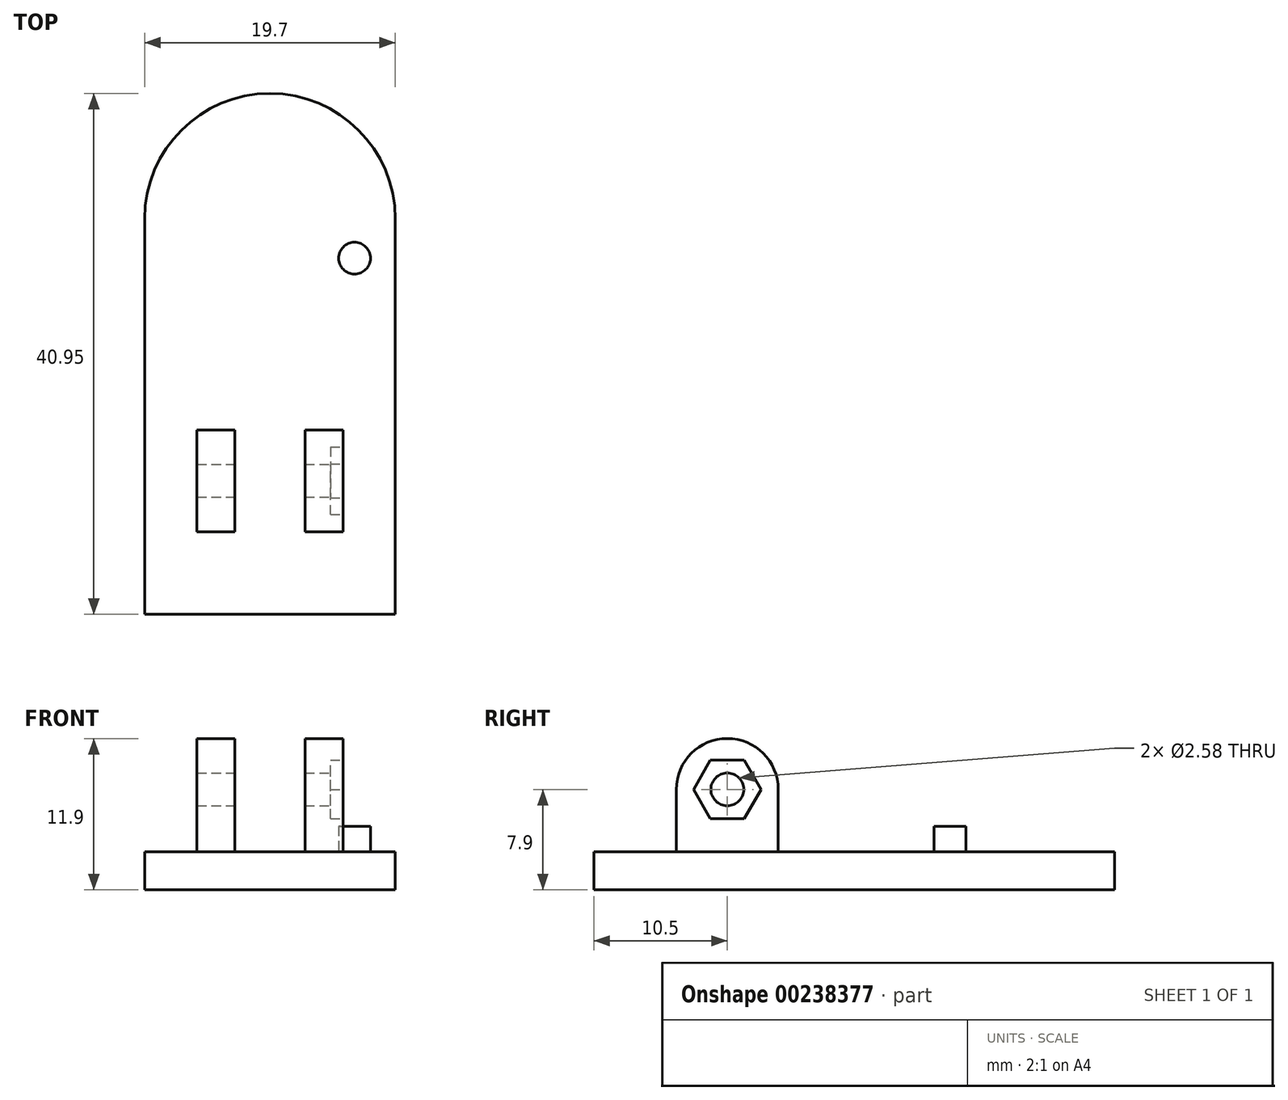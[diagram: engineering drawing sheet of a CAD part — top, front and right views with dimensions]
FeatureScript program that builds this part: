
annotation { "Feature Type Name" : "Feature", "Feature Type Description" : "" }
export const myFeature = defineFeature(function(context is Context, id is Id, definition is map)
    precondition{}
    {
        {
            var Q0;
            Q0=qCreatedBy(makeId("Top.planeOp"),FACE);
            var sketch = newSketch(context, id + "F0", { "sketchPlane" : qUnion([Q0])});
            skCircle(sketch, "E0", {"center": v(0, 0) * mm, "radius": 9.35 * mm});
            skLineSegment(sketch, "E1", {"start": v(-9.35, 0) * mm, "end": v(-9.35, -30.6) * mm});
            skLineSegment(sketch, "E2", {"start": v(9.35, 0) * mm, "end": v(9.35, -30.6) * mm});
            skLineSegment(sketch, "E3", {"start": v(9.35, -30.6) * mm, "end": v(-9.35, -30.6) * mm});
            skLineSegment(sketch, "E4", {"start": v(-5.75, -24.6) * mm, "end": v(-2.75, -24.6) * mm});
            skLineSegment(sketch, "E5.0", {"start": v(5.75, -16.6) * mm, "end": v(5.75, -24.6) * mm});
            skLineSegment(sketch, "E6.trimOffspring", {"start": v(-5.75, -16.6) * mm, "end": v(-5.75, -24.6) * mm});
            skLineSegment(sketch, "E7.0", {"start": v(-2.75, -16.6) * mm, "end": v(-2.75, -24.6) * mm});
            skLineSegment(sketch, "E8.0", {"start": v(2.75, -16.6) * mm, "end": v(2.75, -24.6) * mm});
            skLineSegment(sketch, "E9.trimOffspring", {"start": v(2.75, -16.6) * mm, "end": v(5.75, -16.6) * mm});
            skPoint(sketch, "E10.orphan", {"position": v(9.35, -16.6) * mm});
            skPoint(sketch, "E11.trimOffspring.end.orphan", {"position": v(0, 9.35) * mm});
            skLineSegment(sketch, "E12.trimOffspring", {"start": v(2.75, -24.6) * mm, "end": v(5.75, -24.6) * mm});
            skPoint(sketch, "E13.start.orphan", {"position": v(0, -30.6) * mm});
            skPoint(sketch, "E14.orphan", {"position": v(-9.35, -24.6) * mm});
            skLineSegment(sketch, "E15", {"start": v(-5.75, -16.6) * mm, "end": v(-2.75, -16.6) * mm});
            skSolve(sketch);
        }
        {
            var Q0;
            Q0=makeQuery(id+"F0.imprint","IMPRINT",FACE,{"disambiguationData":[TD([[makeQuery(id+"F0.imprint","IMPRINT",EDGE,{"derivedFrom":sQuery(id+"F0.wireOp",EDGE,"E5.0")}),-1.0]])]});
            var Q1;
            {var subQ0=sQuery(id+"F0.wireOp",EDGE,"E0");var subQ1=makeQuery(id+"F0.imprint","INTERSECT",VERTEX,{"derivedFrom":[subQ0,sQuery(id+"F0.wireOp",EDGE,"E1")]});Q1=makeQuery(id+"F0.imprint","IMPRINT",FACE,{"disambiguationData":[TD([[makeQuery(id+"F0.imprint","IMPRINT",EDGE,{"disambiguationData":[TD([[subQ1,1.0]])],"derivedFrom":subQ0}),1.0]])]});}
            var Q2;
            {var subQ1=sQuery(id+"F0.wireOp",EDGE,"E1");Q2=makeQuery(id+"F0.imprint","IMPRINT",FACE,{"disambiguationData":[TD([[makeQuery(id+"F0.imprint","IMPRINT",EDGE,{"derivedFrom":subQ1}),1.0]])]});}
            var Q3;
            Q3=makeQuery(id+"F0.imprint","IMPRINT",FACE,{"disambiguationData":[TD([[makeQuery(id+"F0.imprint","IMPRINT",EDGE,{"derivedFrom":sQuery(id+"F0.wireOp",EDGE,"E4")}),1.0]])]});
            extrude(context, id + "F1", {"entities" : qUnion([Q0, Q1, Q2, Q3]), "oppositeDirection" : true, "depth" : 3 * mm});
        }
        {
            var Q0;
            Q0=makeQuery(id+"F0.imprint","IMPRINT",FACE,{"disambiguationData":[TD([[makeQuery(id+"F0.imprint","IMPRINT",EDGE,{"derivedFrom":sQuery(id+"F0.wireOp",EDGE,"E5.0")}),-1.0]])]});
            extrude(context, id + "F2", {"entities" : qUnion([Q0]), "operationType" : NewBodyOperationType.ADD, "depth" : 4.9 * mm});
        }
        {
            var Q0;
            Q0=makeQuery(id+"F0.imprint","IMPRINT",FACE,{"disambiguationData":[TD([[makeQuery(id+"F0.imprint","IMPRINT",EDGE,{"derivedFrom":sQuery(id+"F0.wireOp",EDGE,"E4")}),1.0]])]});
            extrude(context, id + "F3", {"entities" : qUnion([Q0]), "operationType" : NewBodyOperationType.ADD, "depth" : 4.9 * mm});
        }
        {
            var Q0;
            Q0=makeQuery(id+"F3.opExtrude","SWEPT_FACE",FACE,{"disambiguationData":[OSD([sQuery(id+"F0.wireOp",EDGE,"E6.trimOffspring")])]});
            var sketch = newSketch(context, id + "F4", { "sketchPlane" : qUnion([Q0])});
            skCircle(sketch, "E16", {"center": v(20.6, 4.9) * mm, "radius": 4 * mm});
            skSolve(sketch);
        }
        {
            var Q0;
            {var subQ1=sQuery(id+"F0.wireOp",EDGE,"E6.trimOffspring");var subQ2=makeQuery(id+"F3.opExtrude","CAP_EDGE",EDGE,{"disambiguationData":[OSD([subQ1])],"isStart":false});Q0=makeQuery(id+"F4.imprint","IMPRINT",FACE,{"disambiguationData":[TD([[makeQuery(id+"F4.imprint","IMPRINT",EDGE,{"derivedFrom":subQ2}),1.0]])]});}
            extrude(context, id + "F5", {"entities" : qUnion([Q0]), "operationType" : NewBodyOperationType.ADD, "oppositeDirection" : true, "depth" : 3 * mm});
        }
        {
            var Q0;
            Q0=makeQuery(id+"F2.opExtrude","SWEPT_FACE",FACE,{"disambiguationData":[OSD([sQuery(id+"F0.wireOp",EDGE,"E5.0")])]});
            var sketch = newSketch(context, id + "F6", { "sketchPlane" : qUnion([Q0])});
            skCircle(sketch, "E17", {"center": v(-20.6, 4.9) * mm, "radius": 4 * mm});
            skCircle(sketch, "E18", {"center": v(-20.6, 4.9) * mm, "radius": 1.29 * mm});
            skCircle(sketch, "E19", {"center": v(-20.6, 4.9) * mm, "radius": 2.66 * mm, "construction": true});
            skLineSegment(sketch, "E20.0", {"start": v(-17.94, 4.9) * mm, "end": v(-19.27, 2.6) * mm});
            skLineSegment(sketch, "E20.1", {"start": v(-19.27, 2.6) * mm, "end": v(-21.93, 2.6) * mm});
            skLineSegment(sketch, "E20.2", {"start": v(-21.93, 2.6) * mm, "end": v(-23.26, 4.9) * mm});
            skLineSegment(sketch, "E20.3", {"start": v(-23.26, 4.9) * mm, "end": v(-21.93, 7.2) * mm});
            skLineSegment(sketch, "E20.4", {"start": v(-21.93, 7.2) * mm, "end": v(-19.27, 7.2) * mm});
            skLineSegment(sketch, "E20.5", {"start": v(-19.27, 7.2) * mm, "end": v(-17.94, 4.9) * mm});
            skSolve(sketch);
        }
        {
            var Q0;
            {var subQ1=sQuery(id+"F0.wireOp",EDGE,"E5.0");var subQ2=makeQuery(id+"F2.opExtrude","CAP_EDGE",EDGE,{"disambiguationData":[OSD([subQ1])],"isStart":false});Q0=makeQuery(id+"F6.imprint","IMPRINT",FACE,{"disambiguationData":[TD([[makeQuery(id+"F6.imprint","IMPRINT",EDGE,{"derivedFrom":subQ2}),-1.0]])]});}
            extrude(context, id + "F7", {"entities" : qUnion([Q0]), "operationType" : NewBodyOperationType.ADD, "oppositeDirection" : true, "depth" : 3 * mm});
        }
        {
            var Q0;
            {var subQ0=sQuery(id+"F6.wireOp",EDGE,"E18");var subQ1=makeQuery(id+"F2.opExtrude","CAP_EDGE",EDGE,{"disambiguationData":[OSD([sQuery(id+"F0.wireOp",EDGE,"E5.0")])],"isStart":false});var subQ2=makeQuery(id+"F6.imprint","INTERSECT",VERTEX,{"disambiguationData":[OD(0.0)],"derivedFrom":[subQ1,subQ0]});Q0=makeQuery(id+"F6.imprint","IMPRINT",FACE,{"disambiguationData":[TD([[makeQuery(id+"F6.imprint","IMPRINT",EDGE,{"disambiguationData":[TD([[subQ2,-1.0]])],"derivedFrom":subQ0}),1.0]])]});}
            var Q1;
            {var subQ0=sQuery(id+"F6.wireOp",EDGE,"E18");var subQ1=makeQuery(id+"F2.opExtrude","CAP_EDGE",EDGE,{"disambiguationData":[OSD([sQuery(id+"F0.wireOp",EDGE,"E5.0")])],"isStart":false});var subQ2=makeQuery(id+"F6.imprint","INTERSECT",VERTEX,{"disambiguationData":[OD(0.0)],"derivedFrom":[subQ1,subQ0]});Q1=makeQuery(id+"F6.imprint","IMPRINT",FACE,{"disambiguationData":[TD([[makeQuery(id+"F6.imprint","IMPRINT",EDGE,{"disambiguationData":[TD([[subQ2,1.0]])],"derivedFrom":subQ0}),1.0]])]});}
            extrude(context, id + "F8", {"entities" : qUnion([Q0, Q1]), "operationType" : NewBodyOperationType.REMOVE, "oppositeDirection" : true, "depth" : 25 * mm});
        }
        {
            var Q0;
            {var subQ0=sQuery(id+"F6.wireOp",EDGE,"E20.3");Q0=makeQuery(id+"F6.imprint","IMPRINT",FACE,{"disambiguationData":[TD([[makeQuery(id+"F6.imprint","IMPRINT",EDGE,{"derivedFrom":subQ0}),-1.0]])]});}
            var Q1;
            {var subQ1=sQuery(id+"F6.wireOp",EDGE,"E20.0");Q1=makeQuery(id+"F6.imprint","IMPRINT",FACE,{"disambiguationData":[TD([[makeQuery(id+"F6.imprint","IMPRINT",EDGE,{"derivedFrom":subQ1}),-1.0]])]});}
            extrude(context, id + "F9", {"entities" : qUnion([Q0, Q1]), "operationType" : NewBodyOperationType.REMOVE, "oppositeDirection" : true, "depth" : 1 * mm});
        }
        {
            var Q0;
            {var subQ0=sQuery(id+"F0.wireOp",EDGE,"E0");var subQ1=makeQuery(id+"F0.imprint","INTERSECT",VERTEX,{"derivedFrom":[subQ0,sQuery(id+"F0.wireOp",EDGE,"E1")]});Q0=makeQuery(id+"F0.imprint","IMPRINT",FACE,{"disambiguationData":[TD([[makeQuery(id+"F0.imprint","IMPRINT",EDGE,{"disambiguationData":[TD([[subQ1,1.0]])],"derivedFrom":subQ0}),1.0]])]});}
            var sketch = newSketch(context, id + "F10", { "sketchPlane" : qUnion([Q0])});
            skLineSegment(sketch, "E21.0", {"start": v(-9.35, 0) * mm, "end": v(-9.35, -30.6) * mm});
            skArc(sketch, "E21.1", {"start": v(9.35, 0) * mm, "mid": v(0, 9.35) * mm, "end": v(-9.35, 0) * mm});
            skLineSegment(sketch, "E21.2", {"start": v(9.35, 0) * mm, "end": v(9.35, -30.6) * mm});
            skLineSegment(sketch, "E21.3", {"start": v(9.35, -30.6) * mm, "end": v(-9.35, -30.6) * mm});
            skLineSegment(sketch, "E22.0", {"start": v(9.85, 0) * mm, "end": v(9.85, -31.1) * mm});
            skLineSegment(sketch, "E22.1", {"start": v(9.85, -31.1) * mm, "end": v(-9.85, -31.1) * mm});
            skLineSegment(sketch, "E22.2", {"start": v(-9.85, 0) * mm, "end": v(-9.85, -31.1) * mm});
            skArc(sketch, "E23.0", {"start": v(9.85, 0) * mm, "mid": v(0, 9.85) * mm, "end": v(-9.85, 0) * mm});
            skSolve(sketch);
        }
        {
            var Q0;
            Q0=makeQuery(id+"F10.imprint","IMPRINT",FACE,{"disambiguationData":[TD([[makeQuery(id+"F10.imprint","IMPRINT",EDGE,{"derivedFrom":sQuery(id+"F10.wireOp",EDGE,"E21.0")}),-1.0]])]});
            extrude(context, id + "F11", {"entities" : qUnion([Q0]), "operationType" : NewBodyOperationType.ADD, "oppositeDirection" : true, "depth" : 3 * mm});
        }
        {
            var Q0;
            Q0=makeQuery(id+"F5.boolean.opBoolean","MERGE",FACE,{"derivedFrom":[makeQuery(id+"F3.opExtrude","SWEPT_FACE",FACE,{"disambiguationData":[OSD([sQuery(id+"F0.wireOp",EDGE,"E7.0")])]}),makeQuery(id+"F5.opExtrude","CAP_FACE",FACE,{"disambiguationData":[OSD([sQuery(id+"F0.wireOp",EDGE,"E6.trimOffspring"),sQuery(id+"F4.wireOp",EDGE,"E16")])],"isStart":false})]});
            var sketch = newSketch(context, id + "F12", { "sketchPlane" : qUnion([Q0])});
            skCircle(sketch, "E24", {"center": v(-20.6, 4.9) * mm, "radius": 1.86 * mm});
            skSolve(sketch);
        }
        {
            var Q0;
            Q0=qSketchRegion(id+"F12",true);
            extrude(context, id + "F13", {"entities" : qUnion([Q0]), "operationType" : NewBodyOperationType.ADD, "oppositeDirection" : true, "depth" : 1 * mm});
        }
        {
            var Q0;
            Q0=makeQuery(id+"F7.boolean.opBoolean","MERGE",FACE,{"derivedFrom":[makeQuery(id+"F2.opExtrude","SWEPT_FACE",FACE,{"disambiguationData":[OSD([sQuery(id+"F0.wireOp",EDGE,"E8.0")])]}),makeQuery(id+"F7.opExtrude","CAP_FACE",FACE,{"disambiguationData":[OSD([sQuery(id+"F0.wireOp",EDGE,"E5.0"),sQuery(id+"F6.wireOp",EDGE,"E17"),sQuery(id+"F6.wireOp",EDGE,"E18")])],"isStart":false})]});
            var sketch = newSketch(context, id + "F14", { "sketchPlane" : qUnion([Q0])});
            skCircle(sketch, "E25", {"center": v(20.6, 4.9) * mm, "radius": 1.9 * mm});
            skSolve(sketch);
        }
        {
            var Q0;
            Q0=qSketchRegion(id+"F14",true);
            extrude(context, id + "F15", {"entities" : qUnion([Q0]), "operationType" : NewBodyOperationType.ADD, "oppositeDirection" : true, "depth" : 1 * mm});
        }
        {
            var Q0;
            Q0=makeQuery(id+"F10.imprint","IMPRINT",FACE,{"disambiguationData":[TD([[makeQuery(id+"F10.imprint","IMPRINT",EDGE,{"derivedFrom":sQuery(id+"F10.wireOp",EDGE,"E21.0")}),1.0]])]});
            var sketch = newSketch(context, id + "F16", { "sketchPlane" : qUnion([Q0])});
            skLineSegment(sketch, "E26.0", {"start": v(2.75, -16.6) * mm, "end": v(5.75, -16.6) * mm});
            skLineSegment(sketch, "E27", {"start": v(5.75, -16.6) * mm, "end": v(5.75, -3.1) * mm, "construction": true});
            skLineSegment(sketch, "E28", {"start": v(5.75, -3.1) * mm, "end": v(6.65, -3.1) * mm});
            skCircle(sketch, "E29", {"center": v(6.65, -3.1) * mm, "radius": 1.25 * mm});
            skSolve(sketch);
        }
        {
            var Q0;
            Q0=qSketchRegion(id+"F16",true);
            extrude(context, id + "F17", {"entities" : qUnion([Q0]), "operationType" : NewBodyOperationType.ADD, "depth" : 2 * mm});
        }
        {
            var Q0;
            Q0=makeQuery(id+"F13.opExtrude","CAP_FACE",FACE,{"disambiguationData":[OSD([sQuery(id+"F12.wireOp",EDGE,"E24")])],"isStart":false});
            extrude(context, id + "F18", {"entities" : qUnion([Q0]), "operationType" : NewBodyOperationType.REMOVE, "oppositeDirection" : true, "depth" : 25 * mm});
        }
    });
